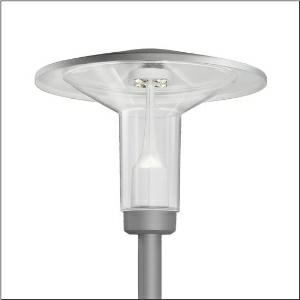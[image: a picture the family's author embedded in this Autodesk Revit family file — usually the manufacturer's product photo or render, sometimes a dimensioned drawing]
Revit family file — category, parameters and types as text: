
# Revit family: laterne_iq___p1_0a_5xa5255nf14h_4412
name_source: partatom
category: Lighting Fixtures
units: mm (PartAtom-declared; Revit-internal decimal feet)

## family parameters
Cut with Voids When Loaded = No
Host = Face
Light Source = No
Part Type = Normal
Room Calculation Point = No
Round Connector Dimension = Use Diameter
Shared = No

## types (1)
- --- (1 x LED, 1510 lm, 11.8 W, 2700K)
    Apparent Load = 12 VA
    CIE Flux Codes = 35 64 91 96 100
    Color Rendering = 70
    Color Temperature = 2700K
    Default Elevation = 1800 mm
    Description = Lantern iQ, mast luminaire, Module 540 iQ-SR, primary light control with 3 zone facetted reflector, of plastic, silver coated, highly specular, structured, primary optical cover: cover, of PMMA, transparent, light distribution: P1.0a, light emission: direct distribution, primary light characteristic: strongly asymmetric, installation type: post-top, LED, High Power LED, rated luminous flux: 1.510lm, luminous efficacy: 128lm/W, light colour: 727, colour temperature: 2700K, control gear: ECG iQ, control: presetting dimming logarithmic, Street-Remote, Auto-Match, Temp-Guard, Lumen-Switch, Night-Set, Smart-Wire, Light-Fading, Desk-Remote (wireless, voltage-free reading and setting of iQ features in the workshop via application-optimized NFC function/RFID function), optimised constant luminous flux control (CLO 2.0), with terminal, 6-pole, max. 2.5mm², mains connection: 220..240V, AC, 50/60Hz, start of lifetime: 12W, end of lifetime: 12W, reduction: 6W, luminaire housing, upper part, of glass-fibre reinforced polyester, coated, Siteco® metallic grey (DB 702S), diameter: 750mm, height: 583mm, spigot size: d x l = 76 x 70mm (post-top) | with reducer (optional accessory) 60 x 70mm, post-top mast mounting element, of diecast aluminium, coated, Siteco® metallic grey (DB 702S), Module 540 iQ-SR, traffic white (RAL 9016), equipment: standard, protection rating (complete): IP65, insulation class (complete): insulation class II (safety insulation), certification: CE, ENEC, VDE, packaging unit: 1 piece

Light Distribution: P1.0a
    Height = 583 mm
    Lamp = 1 x LED
    Lamp Light Flux = 1510 lm
    Lamp Power = 11.8 W
    Lamp count = 1
    Length = 750 mm
    Luminous efficacy = 128 lm/W
    Manufacturer = Siteco
    ModVariant = No
    Model = 5XA5255NF14H
    Number of Poles = 1
    OnlyDefault = Yes
    Power Factor = 1
    Product Name = Laterne iQ | P1.0a
    Product group = mast luminaire | pylon top
    ProductGroupID = 6100
    Protection Class = Protection class II
    Protection Degree = IP 65
    RLX_Detail_Level = 1
    RlxData = <blob elided: 73985 chars, md5=004dccd2>
    Socket = socket
    Standby Power = 0 W
    System Light Flux = 1510 lm
    System Power = 12 W
    Type Comments = factory setting: luminous flux: 100 % | dim-lin: 254 | 472 mA
    Type Image = l_1006050.jpg
    URL = http://relux.com
    VarID = @adj_063217
    Voltage = 0 V
    Weight = 0.00 kg
    Width = 0 mm  [stored 0 ft]

note: [stored X ft] marks values corroborated as IEEE doubles in the binary element streams (Revit-internal decimal feet)

## geometry (parser evidence)
native form markers: Blend x4, Sweep x11
no freeform markers — native parametric forms only
